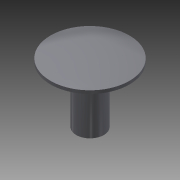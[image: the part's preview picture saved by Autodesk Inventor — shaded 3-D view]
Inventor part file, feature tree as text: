
AUTODESK INVENTOR PART (.ipt)
format: ipt  version: 2013 (Build 170138000, 138)  size: 87,040 bytes
history: native  units: mm (DEFAULTED — no unit token found)
features: sketch x2, reference x2, revolve x1, extrude x1
ambient origin geometry x8: Origin, YZ Plane, XZ Plane, XY Plane, X Axis, Y Axis, Z Axis, Center Point
bodies: Solid1 (feature_tree)
feature tree (6):
  revolve  "Revolution1"  [1 undecoded]
  extrude  "Extrusion1"  [1 undecoded]
  sketch  "Sketch1"  dims[d0=90.0deg d1=3.175mm d2=0.0mm]
  reference  "Reference1"
  reference  "Reference2"
  sketch  "Sketch2"
note: 2 required parameter values undecoded (feature->parameter linkage not recoverable at this tier; creation-order binding heuristic only, values carry confidence <= 0.55)